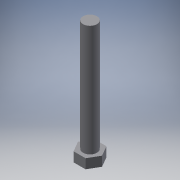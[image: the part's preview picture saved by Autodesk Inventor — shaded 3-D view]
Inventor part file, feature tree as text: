
AUTODESK INVENTOR PART (.ipt)
format: ipt  version: 2016 (Build 200138000, 138)  size: 115,712 bytes
history: native  units: in
note: dims shown in document units (in); Inventor stores cm internally (conversion verified against a paired STEP export)
features: extrude x2, sketch x2
ambient origin geometry x8: Origin, YZ Plane, XZ Plane, XY Plane, X Axis, Y Axis, Z Axis, Center Point
bodies: Solid1 (feature_tree)
feature tree (4):
  extrude  "Extrusion1"  Depth=0.3438in TaperAngle=0.0deg
  extrude  "Extrusion2"  Depth=4.5in TaperAngle=0.0deg
  sketch  "Sketch1"  dims[d0=0.75in d1=0.3438in d2=0.0in]
  sketch  "Sketch2"  dims[d3=0.5in d4=4.5in d5=0.0in]
